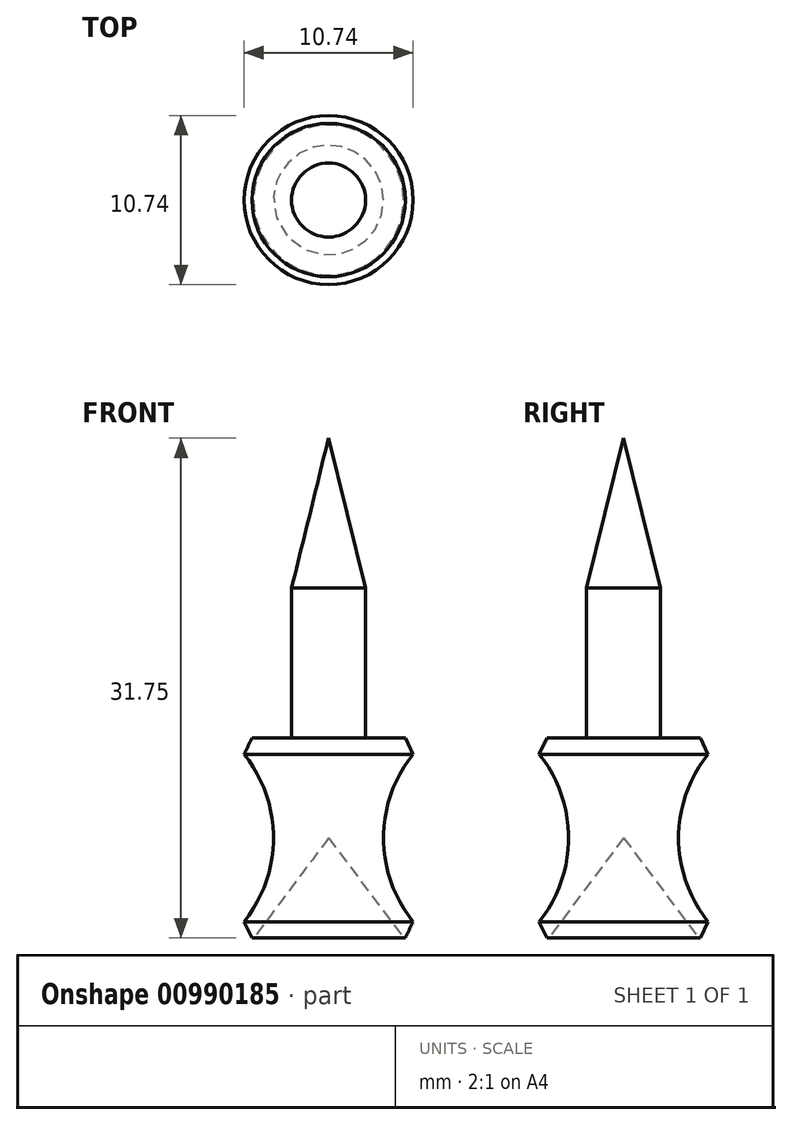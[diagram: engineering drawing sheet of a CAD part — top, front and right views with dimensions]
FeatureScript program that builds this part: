
annotation { "Feature Type Name" : "Feature", "Feature Type Description" : "" }
export const myFeature = defineFeature(function(context is Context, id is Id, definition is map)
    precondition{}
    {
        {
            var Q0;
            Q0=qCreatedBy(makeId("Front.planeOp"),FACE);
            var sketch = newSketch(context, id + "F0", { "sketchPlane" : qUnion([Q0])});
            skLineSegment(sketch, "E0", {"start": v(0, 6.35) * mm, "end": v(4.76, 0) * mm});
            skLineSegment(sketch, "E1", {"start": v(4.76, 0) * mm, "end": v(6.35, 0) * mm});
            skLineSegment(sketch, "E2", {"start": v(6.35, 12.7) * mm, "end": v(2.35, 12.7) * mm});
            skLineSegment(sketch, "E3", {"start": v(2.35, 12.7) * mm, "end": v(2.35, 22.23) * mm});
            skLineSegment(sketch, "E4", {"start": v(2.35, 22.23) * mm, "end": v(0, 31.75) * mm});
            skLineSegment(sketch, "E5", {"start": v(0, 31.75) * mm, "end": v(0, 6.35) * mm});
            skArc(sketch, "E6", {"start": v(6.35, 12.7) * mm, "mid": v(3.5, 6.35) * mm, "end": v(6.35, 0) * mm});
            skSolve(sketch);
        }
        {
            var Q0;
            Q0=makeQuery(id+"F0.imprint","IMPRINT",FACE,{"disambiguationData":[TD([[makeQuery(id+"F0.imprint","IMPRINT",EDGE,{"derivedFrom":sQuery(id+"F0.wireOp",EDGE,"E0")}),1.0]])]});
            var Q1;
            Q1=sQuery(id+"F0.wireOp",EDGE,"E5");
            revolve(context, id + "F1", {"surfaceOperationType" : NewSurfaceOperationType.NEW, "entities" : qUnion([Q0]), "axis" : qUnion([Q1]), "revolveType" : RevolveType.FULL});
        }
        {
            var Q0;
            Q0=makeQuery(id+"F1.opRevolve","SWEPT_EDGE",EDGE,{"disambiguationData":[OSD([sQuery(id+"F0.wireOp",EDGE,"E2"),sQuery(id+"F0.wireOp",EDGE,"E6")])]});
            var Q1;
            Q1=makeQuery(id+"F1.opRevolve","SWEPT_EDGE",EDGE,{"disambiguationData":[OSD([sQuery(id+"F0.wireOp",EDGE,"E1"),sQuery(id+"F0.wireOp",EDGE,"E6")])]});
            chamfer(context, id + "F2", {"entities" : qUnion([Q0, Q1]), "width" : 0.64 * mm, "tangentPropagation" : true});
        }
    });
